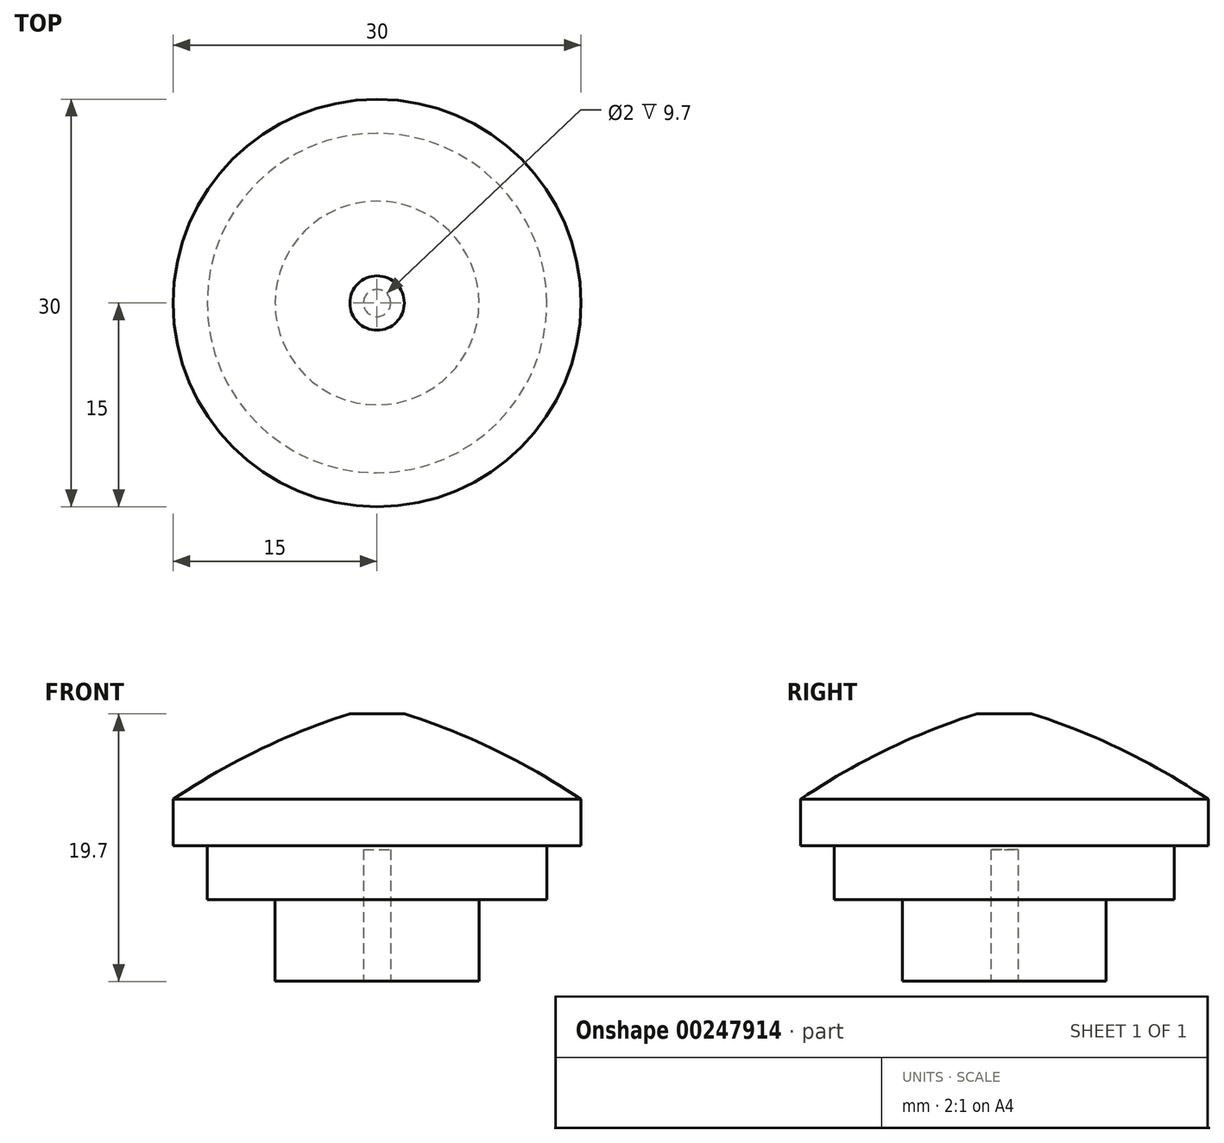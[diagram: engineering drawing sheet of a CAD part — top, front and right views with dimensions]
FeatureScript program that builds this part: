
annotation { "Feature Type Name" : "Feature", "Feature Type Description" : "" }
export const myFeature = defineFeature(function(context is Context, id is Id, definition is map)
    precondition{}
    {
        {
            var Q0;
            Q0=qCreatedBy(makeId("Front.planeOp"),FACE);
            var sketch = newSketch(context, id + "F0", { "sketchPlane" : qUnion([Q0])});
            skLineSegment(sketch, "E0", {"start": v(1, -9.96) * mm, "end": v(7.5, -9.96) * mm});
            skLineSegment(sketch, "E1", {"start": v(7.5, -9.96) * mm, "end": v(7.5, -3.96) * mm});
            skLineSegment(sketch, "E2", {"start": v(7.5, -3.96) * mm, "end": v(12.5, -3.96) * mm});
            skLineSegment(sketch, "E3", {"start": v(12.5, -3.96) * mm, "end": v(12.5, 0.04) * mm});
            skLineSegment(sketch, "E4", {"start": v(12.5, 0.04) * mm, "end": v(15, 0.04) * mm});
            skLineSegment(sketch, "E5", {"start": v(15, 0.04) * mm, "end": v(15, 3.44) * mm});
            skLineSegment(sketch, "E6", {"start": v(2, 9.74) * mm, "end": v(0, 9.74) * mm});
            skLineSegment(sketch, "E7", {"start": v(0, -0.26) * mm, "end": v(0, 9.74) * mm});
            skArc(sketch, "E8", {"start": v(15, 3.44) * mm, "mid": v(8.73, 7.07) * mm, "end": v(2, 9.74) * mm});
            skLineSegment(sketch, "E9", {"start": v(1, -9.96) * mm, "end": v(1, -0.26) * mm});
            skLineSegment(sketch, "E10", {"start": v(1, -0.26) * mm, "end": v(0, -0.26) * mm});
            skPoint(sketch, "E11.orphan", {"position": v(0, -9.96) * mm});
            skSolve(sketch);
        }
        {
            var Q0;
            Q0 = qSketchRegion(id + "F0", true);
            var Q1;
            Q1=sQuery(id+"F0.wireOp",EDGE,"E7");
            revolve(context, id + "F1", {"entities" : qUnion([Q0]), "axis" : qUnion([Q1]), "revolveType" : RevolveType.FULL});
        }
    });
